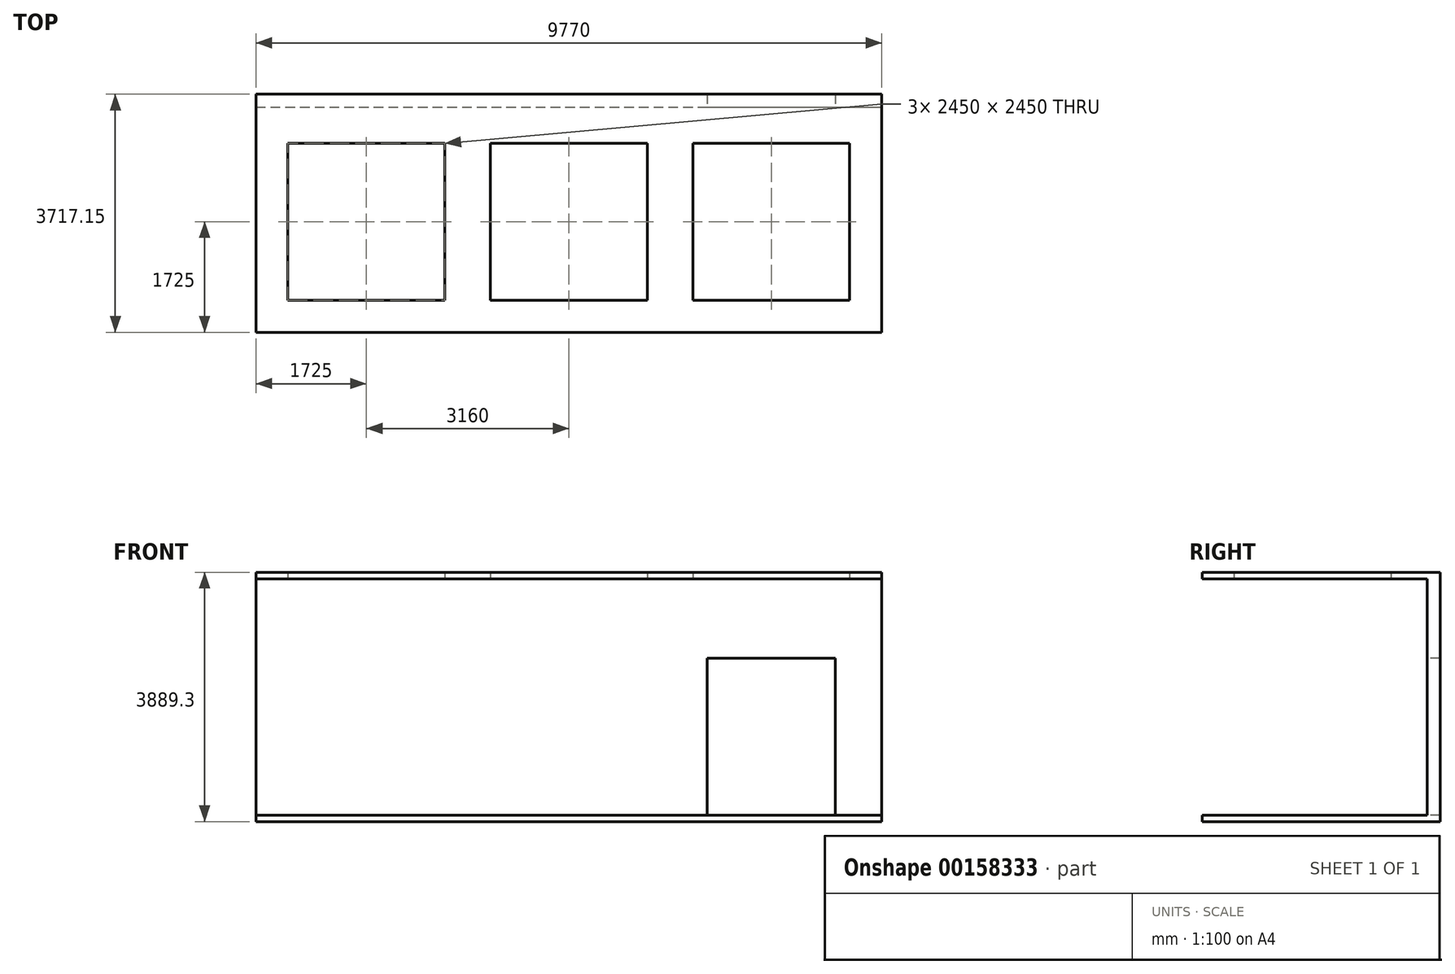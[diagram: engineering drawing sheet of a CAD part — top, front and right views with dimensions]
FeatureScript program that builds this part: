
annotation { "Feature Type Name" : "Feature", "Feature Type Description" : "" }
export const myFeature = defineFeature(function(context is Context, id is Id, definition is map)
    precondition{}
    {
        {
            var Q0;
            Q0=qCreatedBy(makeId("Top.planeOp"),FACE);
            var sketch = newSketch(context, id + "F0", { "sketchPlane" : qUnion([Q0])});
            skLineSegment(sketch, "E0.bottom", {"start": v(-1225, 1225) * mm, "end": v(1225, 1225) * mm});
            skLineSegment(sketch, "E0.top", {"start": v(-1225, -1225) * mm, "end": v(1225, -1225) * mm});
            skLineSegment(sketch, "E0.left", {"start": v(-1225, 1225) * mm, "end": v(-1225, -1225) * mm});
            skLineSegment(sketch, "E0.right", {"start": v(1225, 1225) * mm, "end": v(1225, -1225) * mm});
            skPoint(sketch, "E0.middle", {"position": v(0, 0) * mm});
            skLineSegment(sketch, "E1.bottom", {"start": v(-4385, 1225) * mm, "end": v(-1935, 1225) * mm});
            skLineSegment(sketch, "E1.top", {"start": v(-4385, -1225) * mm, "end": v(-1935, -1225) * mm});
            skLineSegment(sketch, "E1.left", {"start": v(-4385, 1225) * mm, "end": v(-4385, -1225) * mm});
            skLineSegment(sketch, "E1.right", {"start": v(-1935, 1225) * mm, "end": v(-1935, -1225) * mm});
            skPoint(sketch, "E1.middle", {"position": v(-3160, 0) * mm});
            skLineSegment(sketch, "E2.bottom", {"start": v(1935, 1225) * mm, "end": v(4385, 1225) * mm});
            skLineSegment(sketch, "E2.top", {"start": v(1935, -1225) * mm, "end": v(4385, -1225) * mm});
            skLineSegment(sketch, "E2.left", {"start": v(1935, 1225) * mm, "end": v(1935, -1225) * mm});
            skLineSegment(sketch, "E2.right", {"start": v(4385, 1225) * mm, "end": v(4385, -1225) * mm});
            skPoint(sketch, "E2.middle", {"position": v(3160, 0) * mm});
            skLineSegment(sketch, "E3.bottom", {"start": v(-4885, 1792.15) * mm, "end": v(4885, 1792.15) * mm});
            skLineSegment(sketch, "E3.top", {"start": v(-4885, -1725) * mm, "end": v(4885, -1725) * mm});
            skLineSegment(sketch, "E3.left", {"start": v(-4885, 1792.15) * mm, "end": v(-4885, -1725) * mm});
            skLineSegment(sketch, "E3.right", {"start": v(4885, 1792.15) * mm, "end": v(4885, -1725) * mm});
            skPoint(sketch, "E3.middle", {"position": v(0, 33.58) * mm});
            skSolve(sketch);
        }
        {
            var Q0;
            Q0 = qSketchRegion(id + "F0", true);
            extrude(context, id + "F1", {"entities" : qUnion([Q0]), "endBound" : BoundingType.SYMMETRIC, "depth" : 100 * mm});
        }
        {
            var Q0;
            Q0=makeQuery(id+"F1.opExtrude","CAP_FACE",FACE,{"disambiguationData":[OSD([sQuery(id+"F0.wireOp",EDGE,"E0.bottom"),sQuery(id+"F0.wireOp",EDGE,"E0.top"),sQuery(id+"F0.wireOp",EDGE,"E0.left"),sQuery(id+"F0.wireOp",EDGE,"E0.right"),sQuery(id+"F0.wireOp",EDGE,"E1.bottom"),sQuery(id+"F0.wireOp",EDGE,"E1.top"),sQuery(id+"F0.wireOp",EDGE,"E1.left"),sQuery(id+"F0.wireOp",EDGE,"E1.right"),sQuery(id+"F0.wireOp",EDGE,"E2.bottom"),sQuery(id+"F0.wireOp",EDGE,"E2.top"),sQuery(id+"F0.wireOp",EDGE,"E2.left"),sQuery(id+"F0.wireOp",EDGE,"E2.right"),sQuery(id+"F0.wireOp",EDGE,"E3.bottom"),sQuery(id+"F0.wireOp",EDGE,"E3.top"),sQuery(id+"F0.wireOp",EDGE,"E3.left"),sQuery(id+"F0.wireOp",EDGE,"E3.right")])],"isStart":false});
            var sketch = newSketch(context, id + "F2", { "sketchPlane" : qUnion([Q0])});
            skLineSegment(sketch, "E4.bottom", {"start": v(-4885, 1792.15) * mm, "end": v(4885, 1792.15) * mm});
            skLineSegment(sketch, "E4.top", {"start": v(-4885, 1992.15) * mm, "end": v(4885, 1992.15) * mm});
            skLineSegment(sketch, "E4.left", {"start": v(-4885, 1792.15) * mm, "end": v(-4885, 1992.15) * mm});
            skLineSegment(sketch, "E4.right", {"start": v(4885, 1792.15) * mm, "end": v(4885, 1992.15) * mm});
            skSolve(sketch);
        }
        {
            var Q0;
            Q0 = qSketchRegion(id + "F2", true);
            extrude(context, id + "F3", {"entities" : qUnion([Q0]), "operationType" : NewBodyOperationType.ADD, "oppositeDirection" : true, "depth" : 3789.3 * mm});
        }
        {
            var Q0;
            Q0=makeQuery(id+"F3.opExtrude","CAP_FACE",FACE,{"disambiguationData":[OSD([sQuery(id+"F2.wireOp",EDGE,"E4.bottom"),sQuery(id+"F2.wireOp",EDGE,"E4.top"),sQuery(id+"F2.wireOp",EDGE,"E4.left"),sQuery(id+"F2.wireOp",EDGE,"E4.right")])],"isStart":false});
            var sketch = newSketch(context, id + "F4", { "sketchPlane" : qUnion([Q0])});
            skLineSegment(sketch, "E5.bottom", {"start": v(-4885, -1992.15) * mm, "end": v(4885, -1992.15) * mm});
            skLineSegment(sketch, "E5.top", {"start": v(-4885, 1725) * mm, "end": v(4885, 1725) * mm});
            skLineSegment(sketch, "E5.left", {"start": v(-4885, -1992.15) * mm, "end": v(-4885, 1725) * mm});
            skLineSegment(sketch, "E5.right", {"start": v(4885, -1992.15) * mm, "end": v(4885, 1725) * mm});
            skSolve(sketch);
        }
        {
            var Q0;
            Q0 = qSketchRegion(id + "F4", true);
            extrude(context, id + "F5", {"entities" : qUnion([Q0]), "operationType" : NewBodyOperationType.ADD, "depth" : 100 * mm});
        }
        {
            var Q0;
            Q0=makeQuery(id+"F3.opExtrude","SWEPT_FACE",FACE,{"disambiguationData":[OSD([sQuery(id+"F2.wireOp",EDGE,"E4.bottom")])]});
            var sketch = newSketch(context, id + "F6", { "sketchPlane" : qUnion([Q0])});
            skLineSegment(sketch, "E6.bottom", {"start": v(2160, -3739.3) * mm, "end": v(4160, -3739.3) * mm});
            skLineSegment(sketch, "E6.top", {"start": v(2160, -1289.3) * mm, "end": v(4160, -1289.3) * mm});
            skLineSegment(sketch, "E6.left", {"start": v(2160, -3739.3) * mm, "end": v(2160, -1289.3) * mm});
            skLineSegment(sketch, "E6.right", {"start": v(4160, -3739.3) * mm, "end": v(4160, -1289.3) * mm});
            skLineSegment(sketch, "E7.0", {"start": v(1935, -50) * mm, "end": v(4385, -50) * mm, "construction": true});
            skPoint(sketch, "E8", {"position": v(3160, -50) * mm});
            skPoint(sketch, "E9", {"position": v(3160, -1289.3) * mm});
            skSolve(sketch);
        }
        {
            var Q0;
            Q0 = qSketchRegion(id + "F6", true);
            extrude(context, id + "F7", {"entities" : qUnion([Q0]), "operationType" : NewBodyOperationType.REMOVE, "endBound" : BoundingType.UP_TO_NEXT, "oppositeDirection" : true, "depth" : 25 * mm});
        }
    });
